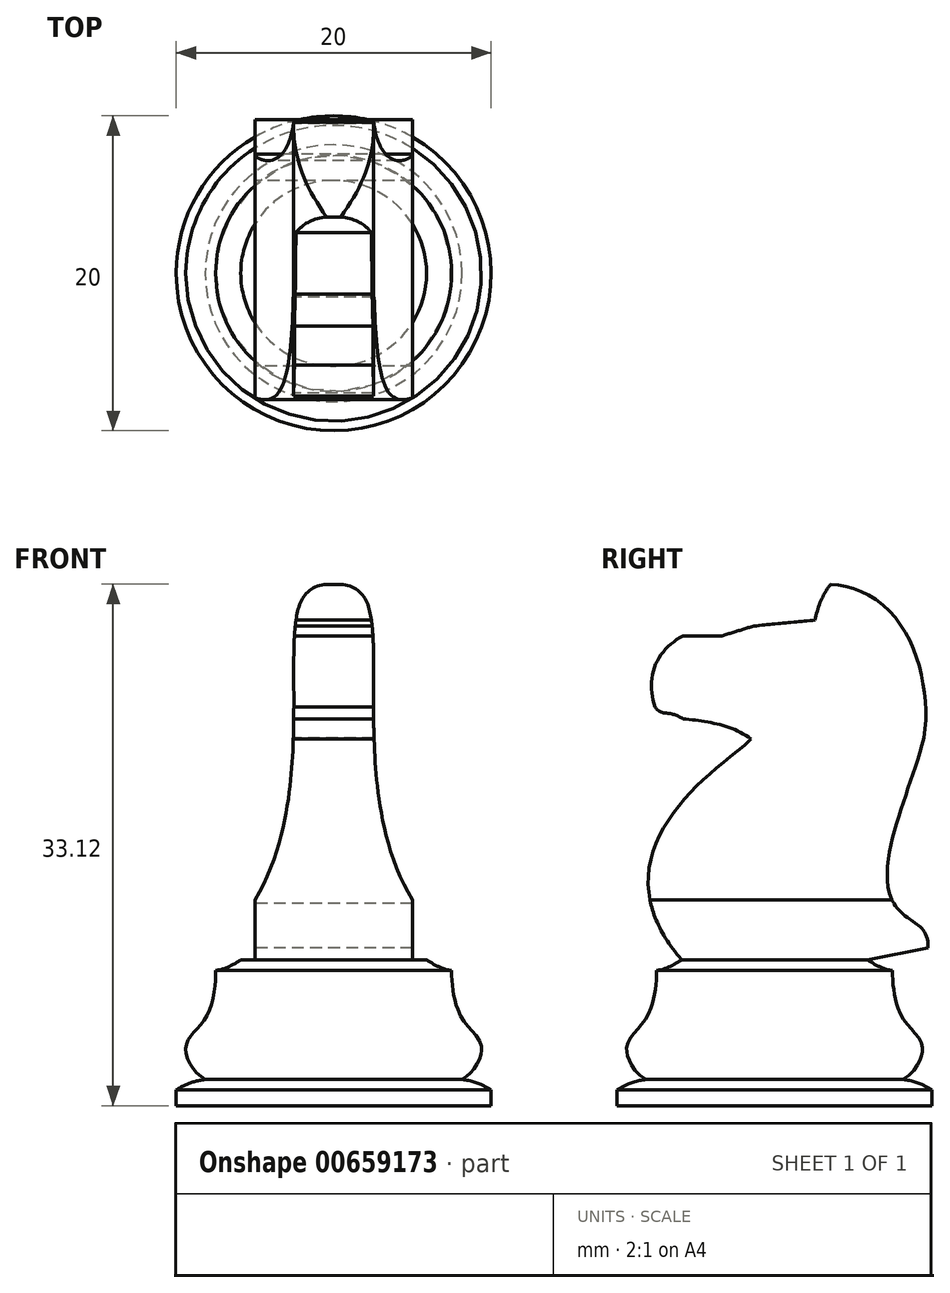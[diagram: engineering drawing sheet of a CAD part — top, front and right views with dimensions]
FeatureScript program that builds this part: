
annotation { "Feature Type Name" : "Feature", "Feature Type Description" : "" }
export const myFeature = defineFeature(function(context is Context, id is Id, definition is map)
    precondition{}
    {
        {
            var Q0;
            Q0=qCreatedBy(makeId("Front.planeOp"),FACE);
            var sketch = newSketch(context, id + "F0", { "sketchPlane" : qUnion([Q0])});
            skLineSegment(sketch, "E0", {"start": v(0, 0) * mm, "end": v(-10, 0) * mm});
            skLineSegment(sketch, "E1", {"start": v(-10, 0) * mm, "end": v(-10, 1) * mm});
            skFitSpline(sketch, "E2", {"points": [v(-10, 1) * mm, v(-8.16, 1.67) * mm], "startDerivative": vector(1.77, 1.13) * mm, "endDerivative": vector(2.24, 0.36) * mm});
            skFitSpline(sketch, "E3", {"points": [v(-8.16, 1.67) * mm, v(-9.38, 3.74) * mm, v(-8.11, 5.62) * mm, v(-7.5, 8.6) * mm], "startDerivative": vector(-6.6, 3.36) * mm, "endDerivative": vector(-0.15, 6.45) * mm});
            skFitSpline(sketch, "E4", {"points": [v(-7.5, 8.6) * mm, v(-5.9, 9.27) * mm], "startDerivative": vector(1.56, 0) * mm, "endDerivative": vector(1.07, 0.72) * mm});
            skLineSegment(sketch, "E5", {"start": v(-5.9, 9.27) * mm, "end": v(0, 9.27) * mm});
            skLineSegment(sketch, "E6", {"start": v(0, 9.27) * mm, "end": v(0, 0) * mm});
            skLineSegment(sketch, "E7", {"start": v(0, -5.17) * mm, "end": v(0, 22.25) * mm});
            skSolve(sketch);
        }
        {
            var Q0;
            Q0=makeQuery(id+"F0.imprint","IMPRINT",FACE,{"disambiguationData":[TD([[makeQuery(id+"F0.imprint","IMPRINT",EDGE,{"derivedFrom":sQuery(id+"F0.wireOp",EDGE,"E0")}),-1.0]])]});
            var Q1;
            Q1=sQuery(id+"F0.wireOp",EDGE,"E7");
            revolve(context, id + "F1", {"entities" : qUnion([Q0]), "axis" : qUnion([Q1]), "revolveType" : RevolveType.FULL});
        }
        {
            var Q0;
            Q0=qCreatedBy(makeId("Right.planeOp"),FACE);
            var sketch = newSketch(context, id + "F2", { "sketchPlane" : qUnion([Q0])});
            skFitSpline(sketch, "E8", {"points": [v(-5.9, 9.27) * mm, v(-1.5, 23.3) * mm], "startDerivative": vector(-19.15, 22.2) * mm, "endDerivative": vector(2.54, 3.53) * mm});
            skFitSpline(sketch, "E9", {"points": [v(-1.5, 23.3) * mm, v(-5.82, 24.58) * mm], "startDerivative": vector(-3.18, 2.51) * mm, "endDerivative": vector(-5.6, 0.6) * mm});
            skFitSpline(sketch, "E10", {"points": [v(-5.82, 24.58) * mm, v(-7.6, 25.33) * mm], "startDerivative": vector(-2.92, 1.84) * mm, "endDerivative": vector(-1.28, 1.9) * mm});
            skFitSpline(sketch, "E11", {"points": [v(-7.6, 25.33) * mm, v(-5.82, 29.84) * mm], "startDerivative": vector(-1.82, 6.07) * mm, "endDerivative": vector(5.05, 2.83) * mm});
            skLineSegment(sketch, "E12", {"start": v(-5.82, 29.84) * mm, "end": v(-3.35, 29.84) * mm});
            skLineSegment(sketch, "E13", {"start": v(-3.35, 29.84) * mm, "end": v(-1.32, 30.47) * mm});
            skLineSegment(sketch, "E14", {"start": v(-1.32, 30.47) * mm, "end": v(2.58, 30.84) * mm});
            skFitSpline(sketch, "E15", {"points": [v(2.58, 30.84) * mm, v(3.57, 33.12) * mm], "startDerivative": vector(0.45, 2.4) * mm, "endDerivative": vector(1.6, 1.88) * mm});
            skFitSpline(sketch, "E16", {"points": [v(3.57, 33.12) * mm, v(9.5, 23.37) * mm], "startDerivative": vector(15.32, -1.1) * mm, "endDerivative": vector(-1.58, -10.4) * mm});
            skFitSpline(sketch, "E17", {"points": [v(9.5, 23.37) * mm, v(7.58, 12.84) * mm], "startDerivative": vector(-2.63, -10.33) * mm, "endDerivative": vector(4.2, -7.05) * mm});
            skFitSpline(sketch, "E18", {"points": [v(7.58, 12.84) * mm, v(9.76, 10.03) * mm], "startDerivative": vector(2.41, -3.94) * mm, "endDerivative": vector(-0.07, -5) * mm});
            skLineSegment(sketch, "E19", {"start": v(-5.9, 9.27) * mm, "end": v(5.9, 9.27) * mm});
            skLineSegment(sketch, "E20", {"start": v(5.9, 9.27) * mm, "end": v(9.76, 10.03) * mm});
            skSolve(sketch);
        }
        {
            var Q0;
            Q0 = qSketchRegion(id + "F2", true);
            extrude(context, id + "F3", {"entities" : qUnion([Q0]), "operationType" : NewBodyOperationType.ADD, "endBound" : BoundingType.SYMMETRIC, "depth" : 10 * mm, "offsetDistance" : 25 * mm});
        }
        {
            var Q0;
            Q0=qCreatedBy(makeId("Front.planeOp"),FACE);
            var sketch = newSketch(context, id + "F4", { "sketchPlane" : qUnion([Q0])});
            skFitSpline(sketch, "E21", {"points": [v(0, 33.14) * mm, v(-2.17, 31.82) * mm, v(-4.56, 13.85) * mm, v(-14.1, -0.46) * mm], "startDerivative": vector(-18.19, -0.14) * mm, "endDerivative": vector(12.1, -31.84) * mm});
            skFitSpline(sketch, "E22.MirrorCS", {"points": [v(0, 33.14) * mm, v(2.17, 31.82) * mm, v(4.56, 13.85) * mm, v(14.1, -0.46) * mm], "startDerivative": vector(18.19, -0.14) * mm, "endDerivative": vector(-12.1, -31.84) * mm});
            skLineSegment(sketch, "E23", {"start": v(-14.1, -0.46) * mm, "end": v(14.1, -0.46) * mm});
            skSolve(sketch);
        }
        {
            var Q0;
            Q0 = qSketchRegion(id + "F4", true);
            extrude(context, id + "F5", {"entities" : qUnion([Q0]), "operationType" : NewBodyOperationType.INTERSECT, "endBound" : BoundingType.SYMMETRIC, "depth" : 50 * mm, "offsetDistance" : 25 * mm});
        }
    });
